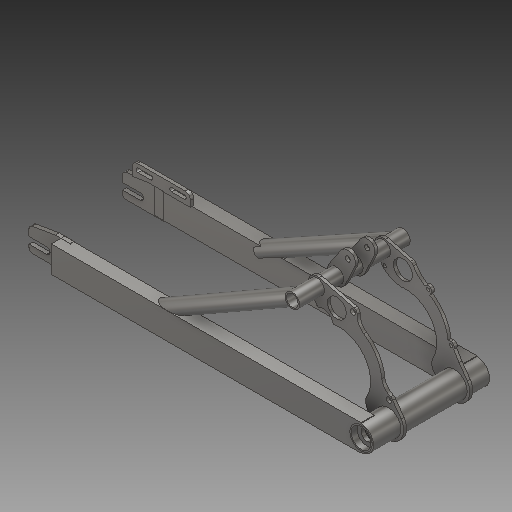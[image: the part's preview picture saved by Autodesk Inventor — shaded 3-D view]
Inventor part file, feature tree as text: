
AUTODESK INVENTOR PART (.ipt)
format: ipt  version: 2019.3 (Build 233278000, 278)  size: 577,536 bytes
history: native  units: mm
features: other x14, extrude x13, sketch x13, reference x8, plane x5, mirror x4, fillet x2, delete_face x2, chamfer x1
ambient origin geometry x8: Origin, YZ Plane, XZ Plane, XY Plane, X Axis, Y Axis, Z Axis, Center Point
bodies: Body1 (feature_tree), Body2 (feature_tree), Body3 (feature_tree), Body4 (feature_tree), Body5 (feature_tree), Body6 (feature_tree), Body7 (feature_tree)
feature tree (62):
  other  "Arms"
  extrude  "Extrusion1"  Depth=20.0mm
  mirror  "Mirror1"
  sketch  "Sketch2"  dims[d3=2.0mm d4=470.0mm d5=0.0mm]
  extrude  "Extrusion4"  Depth=470.0mm TaperAngle=0.0deg
  extrude  "Extrusion2"  Depth=2.0mm
  sketch  "Sketch23"  dims[d78=22.225mm d84=12.5mm]
  extrude  "Extrusion17"  Depth=4.0mm TaperAngle=0.0deg
  plane  "Work Plane19"
  extrude  "Extrusion10"  Depth=4.4mm TaperAngle=0.0deg
  extrude  "Extrusion9"  Depth=2.0mm TaperAngle=0.0deg
  sketch  "3D Sketch3"
  plane  "Work Plane10"
  plane  "Work Plane13"
  extrude  "Extrusion13"  Depth=2.0mm
  extrude  "Extrusion14"  Depth=12.5mm
  mirror  "Mirror6"
  plane  "Work Plane21"
  extrude  "Extrusion16"  Depth=2.0mm
  fillet  "Fillet2"  Radius=2.0mm
  mirror  "Mirror7"
  extrude  "Extrusion18"  Depth=8.0mm
  fillet  "Fillet3"  Radius=12.0mm
  extrude  "Extrusion19"  Depth=4.4mm TaperAngle=0.0deg
  extrude  "Extrusion20"  Depth=10.0mm
  extrude  "Extrusion21"  Depth=6.0mm TaperAngle=0.0deg
  chamfer  "Chamfer1"  Distance=5.5mm
  mirror  "Mirror8"
  delete_face  "Delete Face1"
  delete_face  "Delete Face2"
  sketch  "Sketch1"  dims[d0=40.0mm d1=20.0mm]
  plane  "Work Plane2"
  sketch  "Sketch14"  dims[d6=38.1mm d7=2.0mm]
  sketch  "Sketch15"  dims[d8=155.0mm d9=0.0mm d17=4.0mm d18=0.0mm]
  sketch  "Sketch19"  dims[d19=68.0mm d66=4.4mm d67=0.0mm]
  sketch  "Sketch21"  dims[d69=2.0mm d70=168.0mm d71=0.0mm]
  sketch  "Sketch22"  dims[d72=12.0mm d77=2.0mm]
  reference  "Reference3"
  reference  "Reference4"
  reference  "Reference5"
  reference  "Reference6"
  reference  "Reference8"
  reference  "Reference12"
  other  "FrontMotorPlate"
  other  "ShockPlate"
  other  "BackMotorPlate"
  other  "Dropout"
  sketch  "Sketch25"  dims[d89=4.4mm d90=0.0mm d91=22.225mm d92=2.0mm]
  other  "BrakePlate"
  sketch  "Sketch26"  dims[d93=4.0mm d94=0.0mm d99=8.0mm d100=12.0mm]
  other  "PivotCup"
  sketch  "Sketch27"  dims[d101=14.6125mm d102=4.4mm d103=0.0mm]
  sketch  "Sketch28"  dims[d104=28.575mm d109=10.0mm d110=6.0mm d111=0.0mm d113=5.5mm d115=25.0mm d118=39.9mm d119=78.1mm d122=39.9mm d124=78.1mm d125=51.0mm d127=6.0mm d130=6.0mm d131=5.0mm d132=0.0mm d133=8.0mm d134=9.0mm d135=9.0mm d136=33.9mm d137=15.0mm d138=0.0mm d139=30.0mm d140=9.0mm d141=0.0mm d142=18.0mm d143=9.0mm d144=0.0mm d145=1.0mm d146=2.0mm d147=45.0deg d148=27.0mm d152=19.644428mm d153=19.644428mm d154=5.5mm]
  reference  "Reference18"
  reference  "Reference19"
  other  "<userpath>\Desktop\3dprojects\OpenEmoto\OpenEmoto.iam"
  other  "OpenEmoto.iam"
  other  "BigBlock:1"
  other  "<userpath>\Desktop\3dprojects\VEL Freeride P1\Assembly1.iam"
  other  "Assembly1.iam"
  other  "motor:1"
  other  "Motor:1"
